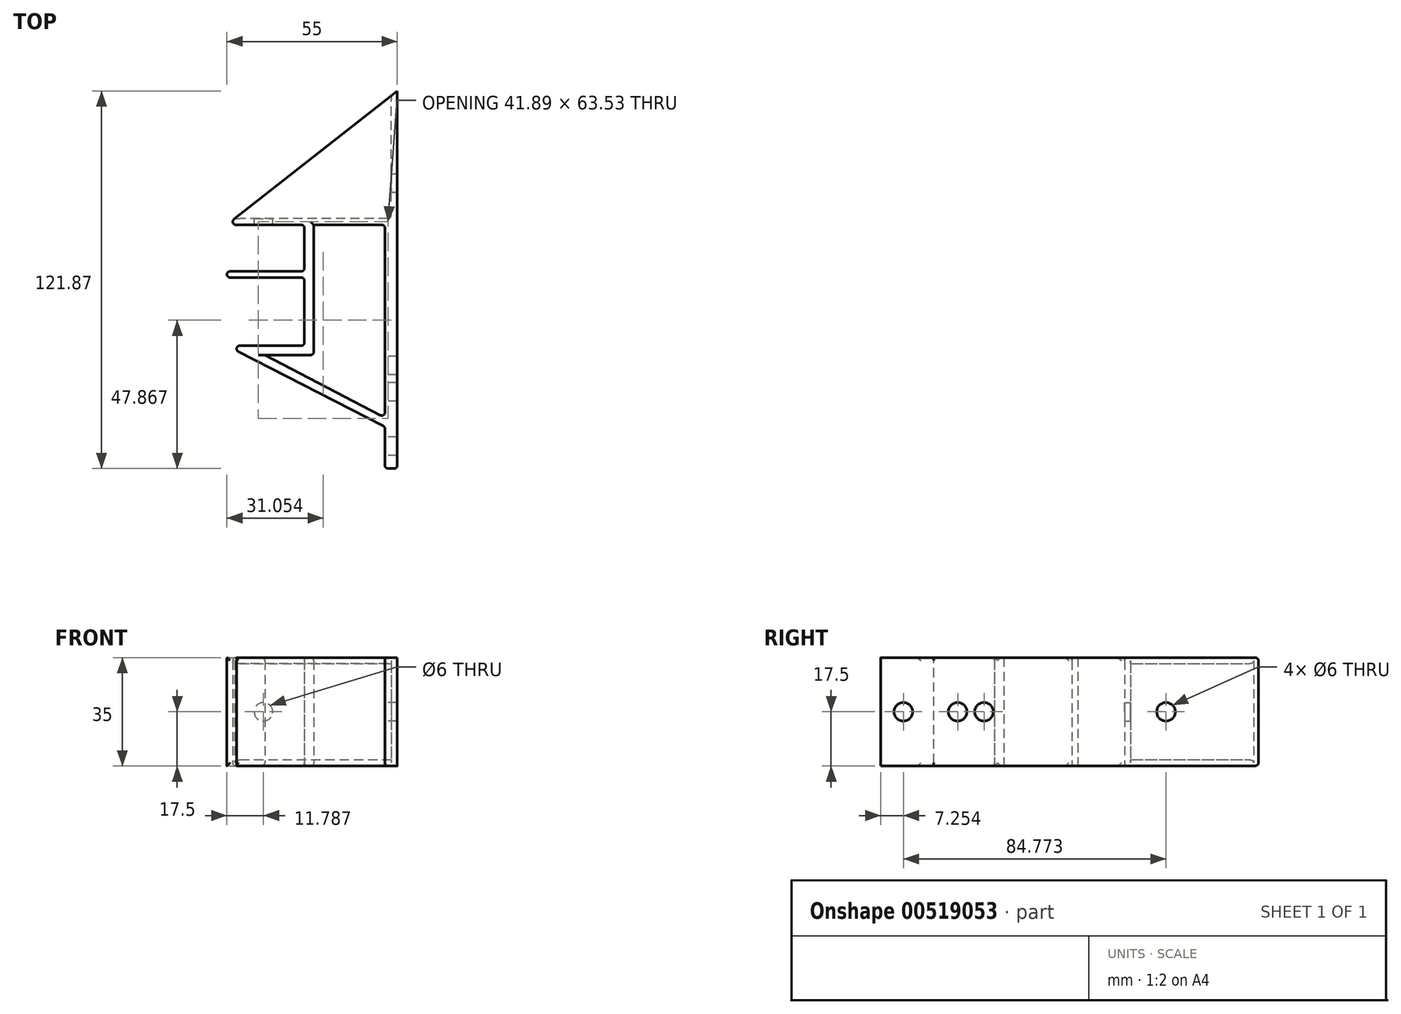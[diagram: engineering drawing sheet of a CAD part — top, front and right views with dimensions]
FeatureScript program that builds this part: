
annotation { "Feature Type Name" : "Feature", "Feature Type Description" : "" }
export const myFeature = defineFeature(function(context is Context, id is Id, definition is map)
    precondition{}
    {
        {
            var Q0;
            Q0=qCreatedBy(makeId("Top.planeOp"),FACE);
            var sketch = newSketch(context, id + "F0", { "sketchPlane" : qUnion([Q0])});
            skLineSegment(sketch, "E0", {"start": v(-25, -35.53) * mm, "end": v(0, -35.53) * mm});
            skLineSegment(sketch, "E1", {"start": v(0, -35.53) * mm, "end": v(0, -13.53) * mm});
            skLineSegment(sketch, "E2", {"start": v(0, -13.53) * mm, "end": v(-25, -13.53) * mm});
            skLineSegment(sketch, "E3", {"start": v(-25, -13.53) * mm, "end": v(-25, -11.53) * mm});
            skLineSegment(sketch, "E4", {"start": v(-25, -11.53) * mm, "end": v(0, -11.53) * mm});
            skLineSegment(sketch, "E5", {"start": v(0, -11.53) * mm, "end": v(0, 3.47) * mm});
            skLineSegment(sketch, "E6", {"start": v(0, 3.47) * mm, "end": v(-25, 3.47) * mm});
            skLineSegment(sketch, "E7", {"start": v(-25, 3.47) * mm, "end": v(26, 43.56) * mm});
            skLineSegment(sketch, "E8", {"start": v(30, -75.16) * mm, "end": v(26, -75.16) * mm});
            skLineSegment(sketch, "E9", {"start": v(26, -75.16) * mm, "end": v(26, -61.7) * mm});
            skLineSegment(sketch, "E10", {"start": v(26, -61.7) * mm, "end": v(-25, -35.53) * mm});
            skLineSegment(sketch, "E11", {"start": v(3, 3.47) * mm, "end": v(26, 3.47) * mm});
            skLineSegment(sketch, "E12", {"start": v(26, 3.47) * mm, "end": v(26, -58.7) * mm});
            skLineSegment(sketch, "E13", {"start": v(3, 3.47) * mm, "end": v(3, -38.53) * mm});
            skLineSegment(sketch, "E14", {"start": v(26, -58.7) * mm, "end": v(-12.73, -38.53) * mm});
            skLineSegment(sketch, "E15", {"start": v(3, -38.53) * mm, "end": v(-12.73, -38.53) * mm});
            skLineSegment(sketch, "E16", {"start": v(30, -75.16) * mm, "end": v(30, 43.56) * mm});
            skLineSegment(sketch, "E17", {"start": v(30, 43.56) * mm, "end": v(30, 50.56) * mm});
            skLineSegment(sketch, "E18", {"start": v(26, 43.56) * mm, "end": v(30, 46.7) * mm});
            skSolve(sketch);
        }
        {
            var Q0;
            Q0=makeQuery(id+"F0.imprint","IMPRINT",FACE,{"disambiguationData":[TD([[makeQuery(id+"F0.imprint","IMPRINT",EDGE,{"derivedFrom":sQuery(id+"F0.wireOp",EDGE,"E0")}),-1.0]])]});
            extrude(context, id + "F1", {"entities" : qUnion([Q0]), "depth" : 35 * mm, "offsetDistance" : 25 * mm});
        }
        {
            var Q0;
            Q0=makeQuery(id+"F1.opExtrude","SWEPT_FACE",FACE,{"disambiguationData":[OSD([sQuery(id+"F0.wireOp",EDGE,"oPx2bCil-G2BR-72yW-5MIQ-B4ESLLbANAro")])]});
            var sketch = newSketch(context, id + "F2", { "sketchPlane" : qUnion([Q0])});
            skLineSegment(sketch, "E19.bottom", {"start": v(-45.56, 2) * mm, "end": v(-63.56, 2) * mm});
            skLineSegment(sketch, "E19.top", {"start": v(-45.56, 33) * mm, "end": v(-63.56, 33) * mm});
            skLineSegment(sketch, "E19.left", {"start": v(-45.56, 2) * mm, "end": v(-45.56, 33) * mm});
            skLineSegment(sketch, "E19.right", {"start": v(-63.56, 2) * mm, "end": v(-63.56, 33) * mm});
            skSolve(sketch);
        }
        {
            var Q0;
            Q0=makeQuery(id+"F1.opExtrude","SWEPT_FACE",FACE,{"disambiguationData":[OSD([sQuery(id+"F0.wireOp",EDGE,"E7")])]});
            shell(context, id + "F3", {"entities" : qUnion([Q0]), "thickness" : 2 * mm});
        }
        {
            var Q0;
            Q0=makeQuery(id+"F3.opShell","OFFSET_FACE",FACE,{"disambiguationData":[OSD([sQuery(id+"F0.wireOp",EDGE,"E16")])]});
            var sketch = newSketch(context, id + "F4", { "sketchPlane" : qUnion([Q0])});
            skCircle(sketch, "E20", {"center": v(-16.87, 17.5) * mm, "radius": 3 * mm});
            skSolve(sketch);
        }
        {
            var Q0;
            Q0 = qSketchRegion(id + "F4", true);
            extrude(context, id + "F5", {"entities" : qUnion([Q0]), "operationType" : NewBodyOperationType.REMOVE, "oppositeDirection" : true, "depth" : 25 * mm, "offsetDistance" : 25 * mm});
        }
        {
            var Q0;
            Q0=makeQuery(id+"F3.opShell","OFFSET_FACE",FACE,{"disambiguationData":[OSD([sQuery(id+"F0.wireOp",EDGE,"E6"),sQuery(id+"F0.wireOp",EDGE,"E11")])]});
            var sketch = newSketch(context, id + "F6", { "sketchPlane" : qUnion([Q0])});
            skCircle(sketch, "E21", {"center": v(13.21, 17.5) * mm, "radius": 3 * mm});
            skSolve(sketch);
        }
        {
            var Q0;
            Q0=makeQuery(id+"F6.imprint","IMPRINT",FACE,{"disambiguationData":[TD([[makeQuery(id+"F6.imprint","IMPRINT",EDGE,{"derivedFrom":sQuery(id+"F6.wireOp",EDGE,"E21")}),1.0]])]});
            extrude(context, id + "F7", {"entities" : qUnion([Q0]), "operationType" : NewBodyOperationType.REMOVE, "oppositeDirection" : true, "depth" : 5.9 * mm, "offsetDistance" : 25 * mm});
        }
        {
            var Q0;
            Q0=makeQuery(id+"F1.opExtrude","CAP_EDGE",EDGE,{"disambiguationData":[OSD([sQuery(id+"F0.wireOp",EDGE,"E7")])],"isStart":false});
            var Q1;
            Q1=makeQuery(id+"F1.opExtrude","CAP_EDGE",EDGE,{"disambiguationData":[OSD([sQuery(id+"F0.wireOp",EDGE,"E7")])],"isStart":true});
            var Q2;
            Q2=makeQuery(id+"F1.opExtrude","SWEPT_EDGE",EDGE,{"disambiguationData":[OSD([sQuery(id+"F0.wireOp",EDGE,"E6"),sQuery(id+"F0.wireOp",EDGE,"E7")])]});
            var Q3;
            Q3=makeQuery(id+"F1.opExtrude","CAP_EDGE",EDGE,{"disambiguationData":[OSD([sQuery(id+"F0.wireOp",EDGE,"oPx2bCil-G2BR-72yW-5MIQ-B4ESLLbANAro")])],"isStart":false});
            var Q4;
            Q4=makeQuery(id+"F1.opExtrude","CAP_EDGE",EDGE,{"disambiguationData":[OSD([sQuery(id+"F0.wireOp",EDGE,"oPx2bCil-G2BR-72yW-5MIQ-B4ESLLbANAro")])],"isStart":true});
            var Q5;
            Q5=makeQuery(id+"F1.opExtrude","SWEPT_EDGE",EDGE,{"disambiguationData":[OSD([sQuery(id+"F0.wireOp",EDGE,"oPx2bCil-G2BR-72yW-5MIQ-B4ESLLbANAro"),sQuery(id+"F0.wireOp",EDGE,"VYgA5tCP-kvoK-BubY-U5EI-h6A52yGNH6Ct")])]});
            var Q6;
            Q6=makeQuery(id+"F1.opExtrude","CAP_EDGE",EDGE,{"disambiguationData":[OSD([sQuery(id+"F0.wireOp",EDGE,"E6")])],"isStart":false});
            var Q7;
            Q7=makeQuery(id+"F1.opExtrude","CAP_EDGE",EDGE,{"disambiguationData":[OSD([sQuery(id+"F0.wireOp",EDGE,"E6")])],"isStart":true});
            var Q8;
            Q8=makeQuery(id+"F1.opExtrude","SWEPT_EDGE",EDGE,{"disambiguationData":[OSD([sQuery(id+"F0.wireOp",EDGE,"E5"),sQuery(id+"F0.wireOp",EDGE,"E6")])]});
            var Q9;
            Q9=makeQuery(id+"F1.opExtrude","SWEPT_EDGE",EDGE,{"disambiguationData":[OSD([sQuery(id+"F0.wireOp",EDGE,"E4"),sQuery(id+"F0.wireOp",EDGE,"E5")])]});
            var Q10;
            Q10=makeQuery(id+"F1.opExtrude","SWEPT_EDGE",EDGE,{"disambiguationData":[OSD([sQuery(id+"F0.wireOp",EDGE,"E1"),sQuery(id+"F0.wireOp",EDGE,"E2")])]});
            var Q11;
            Q11=makeQuery(id+"F1.opExtrude","SWEPT_FACE",FACE,{"disambiguationData":[OSD([sQuery(id+"F0.wireOp",EDGE,"E2")])]});
            var Q12;
            Q12=makeQuery(id+"F1.opExtrude","SWEPT_EDGE",EDGE,{"disambiguationData":[OSD([sQuery(id+"F0.wireOp",EDGE,"E3"),sQuery(id+"F0.wireOp",EDGE,"E4")])]});
            var Q13;
            Q13=makeQuery(id+"F1.opExtrude","SWEPT_EDGE",EDGE,{"disambiguationData":[OSD([sQuery(id+"F0.wireOp",EDGE,"E0"),sQuery(id+"F0.wireOp",EDGE,"E1")])]});
            var Q14;
            Q14=makeQuery(id+"F1.opExtrude","SWEPT_EDGE",EDGE,{"disambiguationData":[OSD([sQuery(id+"F0.wireOp",EDGE,"E0"),sQuery(id+"F0.wireOp",EDGE,"E10")])]});
            var Q15;
            Q15=makeQuery(id+"F1.opExtrude","CAP_EDGE",EDGE,{"disambiguationData":[OSD([sQuery(id+"F0.wireOp",EDGE,"E10")])],"isStart":false});
            var Q16;
            Q16=makeQuery(id+"F1.opExtrude","CAP_EDGE",EDGE,{"disambiguationData":[OSD([sQuery(id+"F0.wireOp",EDGE,"E10")])],"isStart":true});
            var Q17;
            Q17=makeQuery(id+"F1.opExtrude","SWEPT_EDGE",EDGE,{"disambiguationData":[OSD([sQuery(id+"F0.wireOp",EDGE,"E9"),sQuery(id+"F0.wireOp",EDGE,"E10")])]});
            var Q18;
            Q18=makeQuery(id+"F1.opExtrude","CAP_EDGE",EDGE,{"disambiguationData":[OSD([sQuery(id+"F0.wireOp",EDGE,"E13")])],"isStart":false});
            var Q19;
            Q19=makeQuery(id+"F1.opExtrude","CAP_EDGE",EDGE,{"disambiguationData":[OSD([sQuery(id+"F0.wireOp",EDGE,"E14")])],"isStart":false});
            var Q20;
            Q20=makeQuery(id+"F1.opExtrude","CAP_EDGE",EDGE,{"disambiguationData":[OSD([sQuery(id+"F0.wireOp",EDGE,"E12")])],"isStart":false});
            var Q21;
            Q21=makeQuery(id+"F1.opExtrude","CAP_EDGE",EDGE,{"disambiguationData":[OSD([sQuery(id+"F0.wireOp",EDGE,"E11")])],"isStart":false});
            var Q22;
            Q22=makeQuery(id+"F1.opExtrude","CAP_EDGE",EDGE,{"disambiguationData":[OSD([sQuery(id+"F0.wireOp",EDGE,"E13")])],"isStart":true});
            var Q23;
            Q23=makeQuery(id+"F1.opExtrude","CAP_EDGE",EDGE,{"disambiguationData":[OSD([sQuery(id+"F0.wireOp",EDGE,"E11")])],"isStart":true});
            var Q24;
            Q24=makeQuery(id+"F1.opExtrude","CAP_EDGE",EDGE,{"disambiguationData":[OSD([sQuery(id+"F0.wireOp",EDGE,"E12")])],"isStart":true});
            var Q25;
            Q25=makeQuery(id+"F1.opExtrude","CAP_EDGE",EDGE,{"disambiguationData":[OSD([sQuery(id+"F0.wireOp",EDGE,"E14")])],"isStart":true});
            var Q26;
            Q26=makeQuery(id+"F1.opExtrude","SWEPT_EDGE",EDGE,{"disambiguationData":[OSD([sQuery(id+"F0.wireOp",EDGE,"E8"),sQuery(id+"F0.wireOp",EDGE,"E9")])]});
            var Q27;
            Q27=makeQuery(id+"F1.opExtrude","CAP_EDGE",EDGE,{"disambiguationData":[OSD([sQuery(id+"F0.wireOp",EDGE,"hzOoLcAJ-e4uM-ZT2e-sfAq-rAPocIypgjWc")])],"isStart":false});
            var Q28;
            Q28=makeQuery(id+"F1.opExtrude","CAP_EDGE",EDGE,{"disambiguationData":[OSD([sQuery(id+"F0.wireOp",EDGE,"hzOoLcAJ-e4uM-ZT2e-sfAq-rAPocIypgjWc")])],"isStart":true});
            var Q29;
            Q29=makeQuery(id+"F1.opExtrude","SWEPT_EDGE",EDGE,{"disambiguationData":[OSD([sQuery(id+"F0.wireOp",EDGE,"hzOoLcAJ-e4uM-ZT2e-sfAq-rAPocIypgjWc"),sQuery(id+"F0.wireOp",EDGE,"E8")])]});
            var Q30;
            Q30=makeQuery(id+"F1.opExtrude","SWEPT_EDGE",EDGE,{"disambiguationData":[OSD([sQuery(id+"F0.wireOp",EDGE,"VYgA5tCP-kvoK-BubY-U5EI-h6A52yGNH6Ct"),sQuery(id+"F0.wireOp",EDGE,"hzOoLcAJ-e4uM-ZT2e-sfAq-rAPocIypgjWc")])]});
            var Q31;
            Q31=makeQuery(id+"F1.opExtrude","SWEPT_EDGE",EDGE,{"disambiguationData":[OSD([sQuery(id+"F0.wireOp",EDGE,"E13"),sQuery(id+"F0.wireOp",EDGE,"E15")])]});
            var Q32;
            Q32=makeQuery(id+"F1.opExtrude","SWEPT_EDGE",EDGE,{"disambiguationData":[OSD([sQuery(id+"F0.wireOp",EDGE,"E12"),sQuery(id+"F0.wireOp",EDGE,"E14")])]});
            var Q33;
            Q33=makeQuery(id+"F1.opExtrude","SWEPT_EDGE",EDGE,{"disambiguationData":[OSD([sQuery(id+"F0.wireOp",EDGE,"E11"),sQuery(id+"F0.wireOp",EDGE,"E12")])]});
            var Q34;
            {var subQ0=sQuery(id+"F0.wireOp",EDGE,"E7");Q34=makeQuery(id+"F3.opShell","OFFSET_EDGE",EDGE,{"disambiguationData":[OSD([subQ0]),TDD([makeQuery(id+"F1.opExtrude","CAP_EDGE",EDGE,{"disambiguationData":[OSD([subQ0])],"isStart":false})]),OD(0.0)]});}
            var Q35;
            {var subQ0=sQuery(id+"F0.wireOp",EDGE,"E7");Q35=makeQuery(id+"F3.opShell","OFFSET_EDGE",EDGE,{"disambiguationData":[OSD([subQ0]),TDD([makeQuery(id+"F1.opExtrude","CAP_EDGE",EDGE,{"disambiguationData":[OSD([subQ0])],"isStart":true})]),OD(0.0)]});}
            var Q36;
            Q36=makeQuery(id+"F3.opShell","OFFSET_EDGE",EDGE,{"disambiguationData":[OSD([sQuery(id+"F0.wireOp",EDGE,"E11"),sQuery(id+"F0.wireOp",EDGE,"E12")])]});
            fillet(context, id + "F8", {"entities" : qUnion([Q0, Q1, Q2, Q3, Q4, Q5, Q6, Q7, Q8, Q9, Q10, Q11, Q12, Q13, Q14, Q15, Q16, Q17, Q18, Q19, Q20, Q21, Q22, Q23, Q24, Q25, Q26, Q27, Q28, Q29, Q30, Q31, Q32, Q33, Q34, Q35, Q36]), "radius" : 1 * mm, "tangentPropagation" : true, "allowEdgeOverflow" : false});
        }
        {
            var Q0;
            Q0=makeQuery(id+"F1.opExtrude","SWEPT_FACE",FACE,{"disambiguationData":[OSD([sQuery(id+"F0.wireOp",EDGE,"E12")])]});
            var sketch = newSketch(context, id + "F9", { "sketchPlane" : qUnion([Q0])});
            skCircle(sketch, "E22", {"center": v(50.38, 17.5) * mm, "radius": 3 * mm});
            skCircle(sketch, "E23", {"center": v(41.88, 17.5) * mm, "radius": 3 * mm});
            skSolve(sketch);
        }
        {
            var Q0;
            Q0=makeQuery(id+"F9.imprint","IMPRINT",FACE,{"disambiguationData":[TD([[makeQuery(id+"F9.imprint","IMPRINT",EDGE,{"derivedFrom":sQuery(id+"F9.wireOp",EDGE,"E22")}),1.0]])]});
            var Q1;
            Q1=makeQuery(id+"F9.imprint","IMPRINT",FACE,{"disambiguationData":[TD([[makeQuery(id+"F9.imprint","IMPRINT",EDGE,{"derivedFrom":sQuery(id+"F9.wireOp",EDGE,"E23")}),1.0]])]});
            extrude(context, id + "F10", {"entities" : qUnion([Q0, Q1]), "operationType" : NewBodyOperationType.REMOVE, "oppositeDirection" : true, "depth" : 25 * mm, "offsetDistance" : 25 * mm});
        }
        {
            var Q0;
            Q0=makeQuery(id+"F1.opExtrude","SWEPT_FACE",FACE,{"disambiguationData":[OSD([sQuery(id+"F0.wireOp",EDGE,"E9")])]});
            var sketch = newSketch(context, id + "F11", { "sketchPlane" : qUnion([Q0])});
            skCircle(sketch, "E24", {"center": v(67.9, 17.5) * mm, "radius": 3 * mm});
            skSolve(sketch);
        }
        {
            var Q0;
            Q0=makeQuery(id+"F11.imprint","IMPRINT",FACE,{"disambiguationData":[TD([[makeQuery(id+"F11.imprint","IMPRINT",EDGE,{"derivedFrom":sQuery(id+"F11.wireOp",EDGE,"E24")}),1.0]])]});
            extrude(context, id + "F12", {"entities" : qUnion([Q0]), "operationType" : NewBodyOperationType.REMOVE, "oppositeDirection" : true, "depth" : 25 * mm, "offsetDistance" : 25 * mm});
        }
    });
